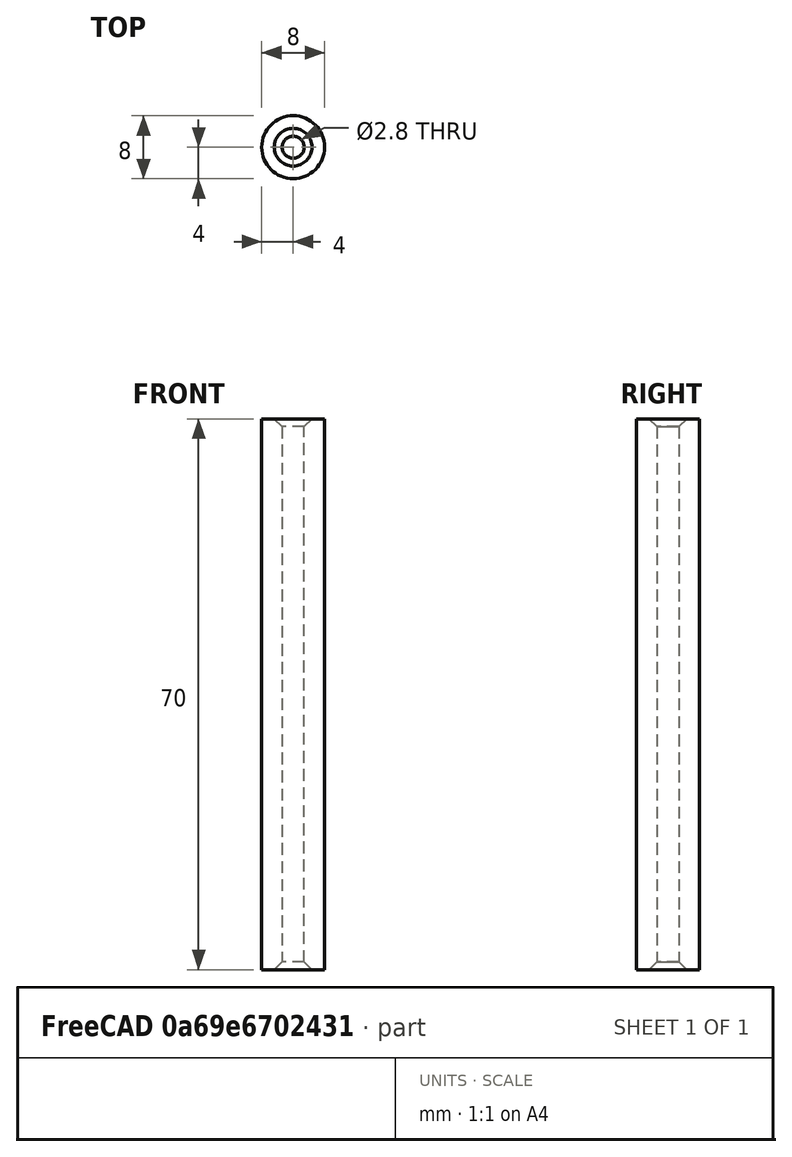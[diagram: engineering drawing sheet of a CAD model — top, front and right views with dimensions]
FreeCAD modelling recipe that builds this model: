
FCSTD DOCUMENT  (FreeCAD 1.0R39109 (Git))
Label: 2_8x8x70mm_spacer_base
License: All rights reserved
LicenseURL: https://en.wikipedia.org/wiki/All_rights_reserved
objects: Sketcher::SketchObject×1, PartDesign::Pad×1, PartDesign::Chamfer×1, PartDesign::Body×1
note: 9 computed .brp shape members not serialized (recipe doc carries the construction recipe); baked Part::Feature solids carry a one-line shape summary decoded from their .brp

FEATURE [Sketcher::SketchObject] Sketch
  ArcFitTolerance = 1e-06
  AttachmentSupport = -> [XY_Plane]
  FullyConstrained = true
  MakeInternals = false
  MapMode = 5
  sketch-geometry (2):
    g0: Circle CenterX=0 CenterY=0 CenterZ=0 NormalX=0 NormalY=0 NormalZ=1 AngleXU=0 Radius=1.4
    g1: Circle CenterX=0 CenterY=0 CenterZ=0 NormalX=0 NormalY=0 NormalZ=1 AngleXU=0 Radius=4
  constraints (4):
    c: Coincident(g0,g-1)
    c: Coincident(g1,g0)
    c: Diameter(g0) = 2.8
    c: Diameter(g1) = 8
FEATURE [PartDesign::Pad] Pad
  Direction = (0,0,1)
  Length = 70
  Length2 = 10
  Profile = -> Sketch
  ReferenceAxis = -> Sketch [N_Axis]
  Refine = true
  Suppressed = false
  Type = 0
FEATURE [PartDesign::Chamfer] Chamfer
  Angle = 45
  Base = -> Pad [Edge6,Edge5]
  BaseFeature = -> Pad
  ChamferType = 0
  FlipDirection = false
  Refine = true
  Size = 1
  Size2 = 1
  SupportTransform = false
  Suppressed = false
  UseAllEdges = false
FEATURE [PartDesign::Body] Body
  AllowCompound = false
  Group = -> [Sketch,Pad,Chamfer]
  Origin = -> Origin
  Tip = -> Chamfer
